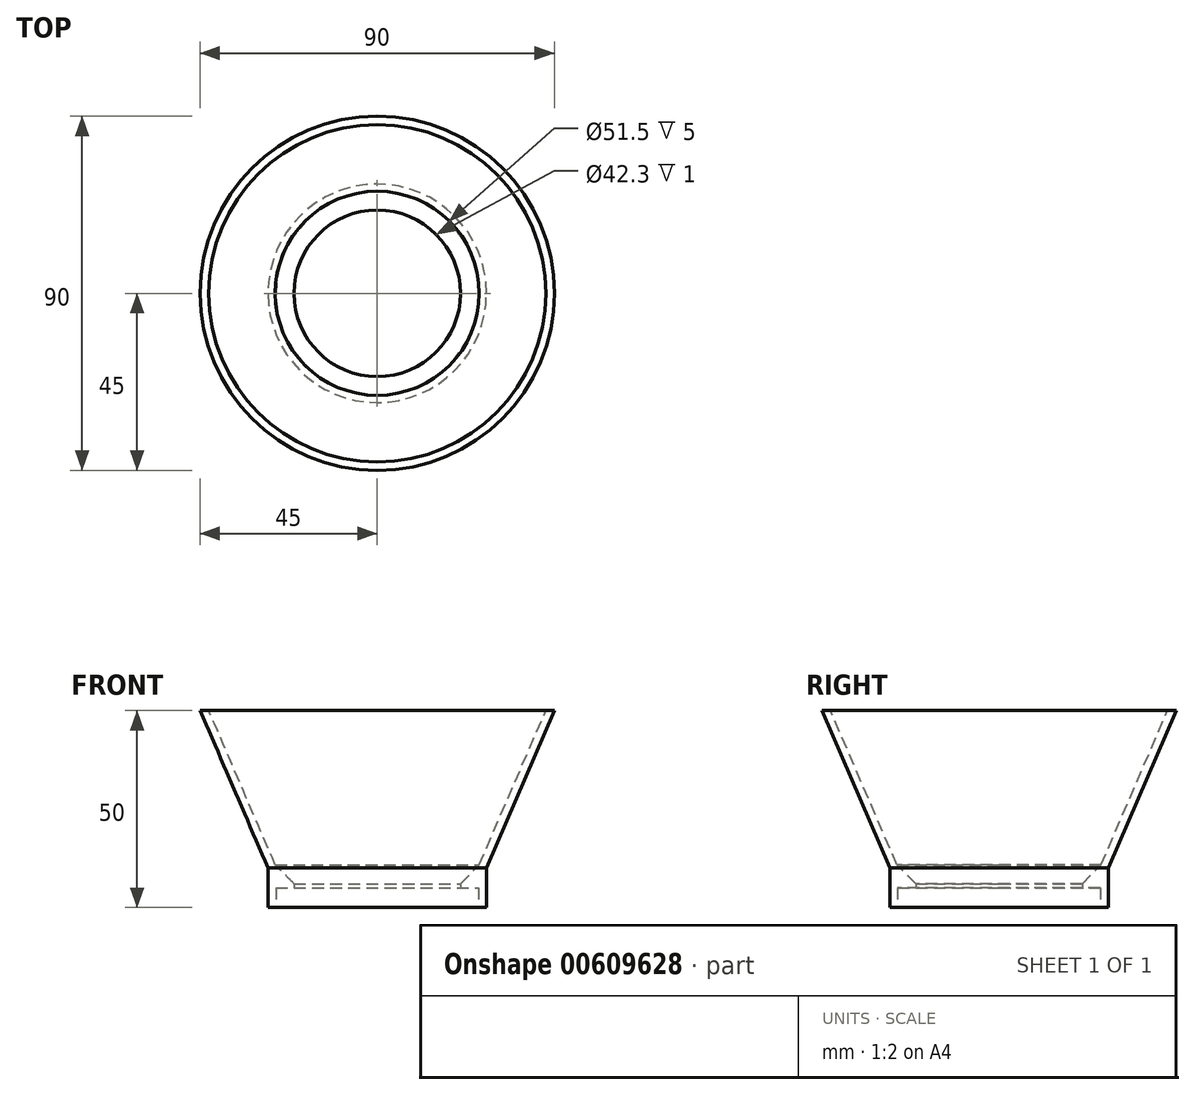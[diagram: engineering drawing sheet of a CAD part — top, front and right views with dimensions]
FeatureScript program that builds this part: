
annotation { "Feature Type Name" : "Feature", "Feature Type Description" : "" }
export const myFeature = defineFeature(function(context is Context, id is Id, definition is map)
    precondition{}
    {
        {
            var Q0;
            Q0=qCreatedBy(makeId("Front.planeOp"),FACE);
            var sketch = newSketch(context, id + "F0", { "sketchPlane" : qUnion([Q0])});
            skLineSegment(sketch, "E0", {"start": v(21.15, 0) * mm, "end": v(25.75, 0) * mm});
            skLineSegment(sketch, "E1", {"start": v(25.75, 0) * mm, "end": v(25.75, -5) * mm});
            skLineSegment(sketch, "E2", {"start": v(25.75, -5) * mm, "end": v(27.75, -5) * mm});
            skLineSegment(sketch, "E3", {"start": v(27.75, -5) * mm, "end": v(27.75, 5) * mm});
            skLineSegment(sketch, "E4", {"start": v(21.15, 0) * mm, "end": v(21.15, 1) * mm});
            skLineSegment(sketch, "E5", {"start": v(27.75, 5) * mm, "end": v(45, 45) * mm});
            skLineSegment(sketch, "E6.0", {"start": v(25.91, 5.8) * mm, "end": v(42.82, 45) * mm});
            skLineSegment(sketch, "E7", {"start": v(45, 45) * mm, "end": v(42.82, 45) * mm});
            skLineSegment(sketch, "E8", {"start": v(21.15, 1) * mm, "end": v(25.91, 5.8) * mm});
            skSolve(sketch);
        }
        {
            var Q0;
            Q0=qCreatedBy(makeId("Top.planeOp"),FACE);
            var sketch = newSketch(context, id + "F1", { "sketchPlane" : qUnion([Q0])});
            skCircle(sketch, "E9", {"center": v(0, 0) * mm, "radius": 12.92 * mm});
            skSolve(sketch);
        }
        {
            var Q0;
            Q0=qSketchRegion(id+"F0",true);
            var Q1;
            Q1=sQuery(id+"F1.wireOp",EDGE,"E9");
            revolve(context, id + "F2", {"entities" : qUnion([Q0]), "axis" : qUnion([Q1]), "revolveType" : RevolveType.FULL});
        }
    });
